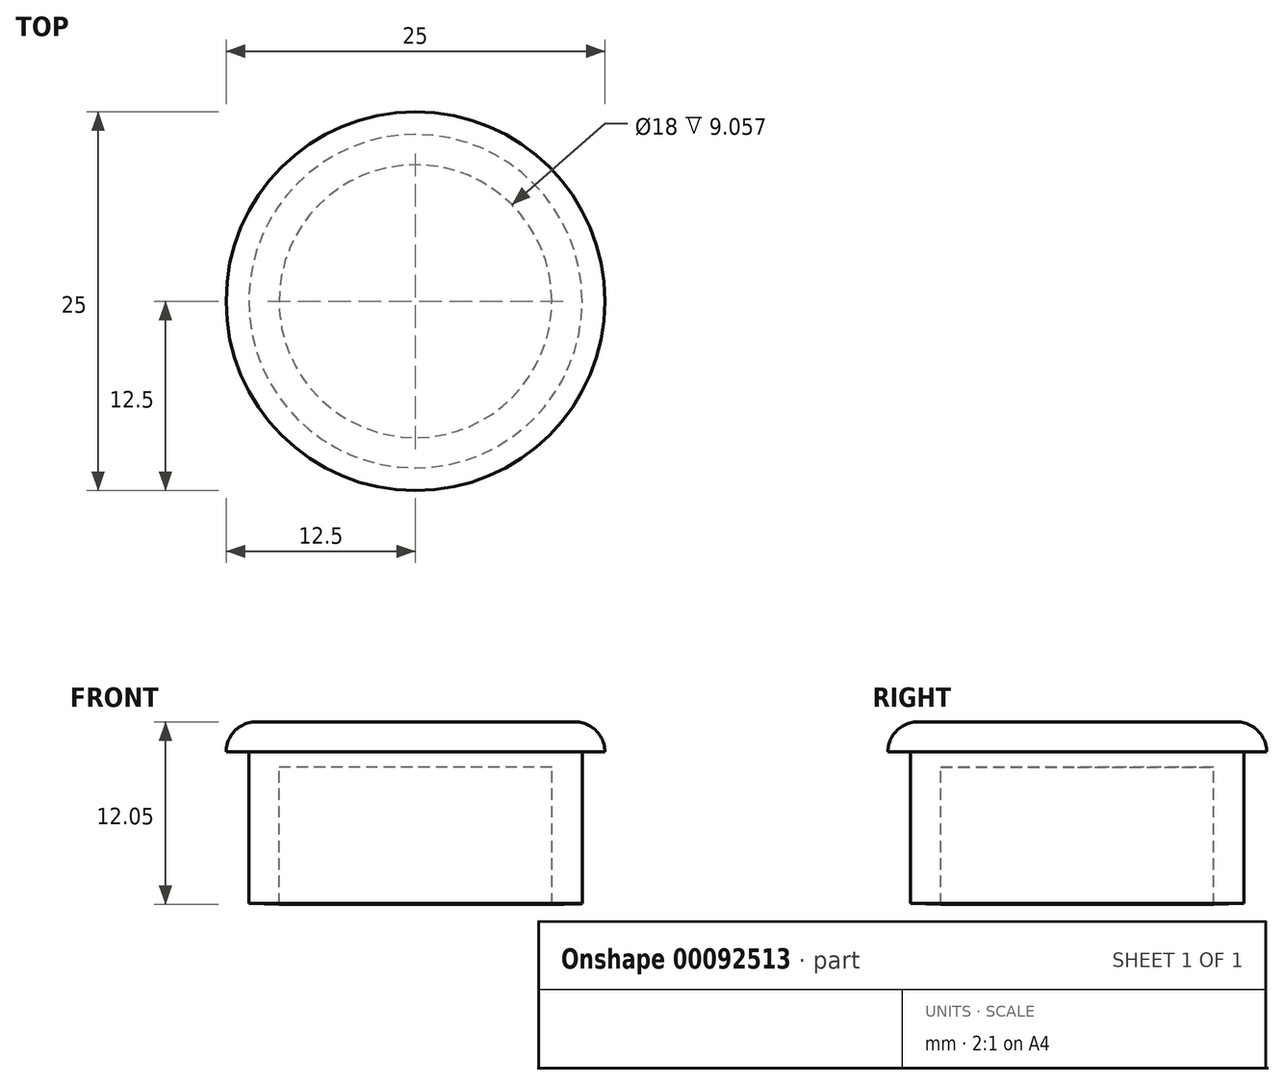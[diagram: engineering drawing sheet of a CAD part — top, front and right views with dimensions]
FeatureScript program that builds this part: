
annotation { "Feature Type Name" : "Feature", "Feature Type Description" : "" }
export const myFeature = defineFeature(function(context is Context, id is Id, definition is map)
    precondition{}
    {
        {
            var Q0;
            Q0=qCreatedBy(makeId("Front.planeOp"),FACE);
            var sketch = newSketch(context, id + "F0", { "sketchPlane" : qUnion([Q0])});
            skLineSegment(sketch, "E0", {"start": v(0, 10.2) * mm, "end": v(-12.5, 10.2) * mm});
            skLineSegment(sketch, "E1", {"start": v(-12.5, 10.2) * mm, "end": v(-12.5, 8.2) * mm});
            skLineSegment(sketch, "E2", {"start": v(-12.5, 8.2) * mm, "end": v(-11, 8.2) * mm});
            skLineSegment(sketch, "E3", {"start": v(-11, 8.2) * mm, "end": v(-11, -1.8) * mm});
            skLineSegment(sketch, "E4", {"start": v(0, 10.2) * mm, "end": v(0, 7.2) * mm});
            skLineSegment(sketch, "E5", {"start": v(0, 7.2) * mm, "end": v(-9, 7.2) * mm});
            skLineSegment(sketch, "E6", {"start": v(-9, 7.2) * mm, "end": v(-9, -1.85) * mm});
            skLineSegment(sketch, "E7", {"start": v(-9, -1.85) * mm, "end": v(-11, -1.8) * mm});
            skSolve(sketch);
        }
        {
            var Q0;
            Q0=makeQuery(id+"F0.imprint","IMPRINT",FACE,{"disambiguationData":[TD([[makeQuery(id+"F0.imprint","IMPRINT",EDGE,{"derivedFrom":sQuery(id+"F0.wireOp",EDGE,"E0")}),1.0]])]});
            var Q1;
            Q1=sQuery(id+"F0.wireOp",EDGE,"E4");
            revolve(context, id + "F1", {"entities" : qUnion([Q0]), "axis" : qUnion([Q1]), "revolveType" : RevolveType.FULL});
        }
        {
            var Q0;
            Q0=makeQuery(id+"F1.opRevolve","SWEPT_FACE",FACE,{"disambiguationData":[OSD([sQuery(id+"F0.wireOp",EDGE,"E0")])]});
            fillet(context, id + "F2", {"entities" : qUnion([Q0]), "radius" : 2 * mm, "tangentPropagation" : true, "allowEdgeOverflow" : false});
        }
    });
